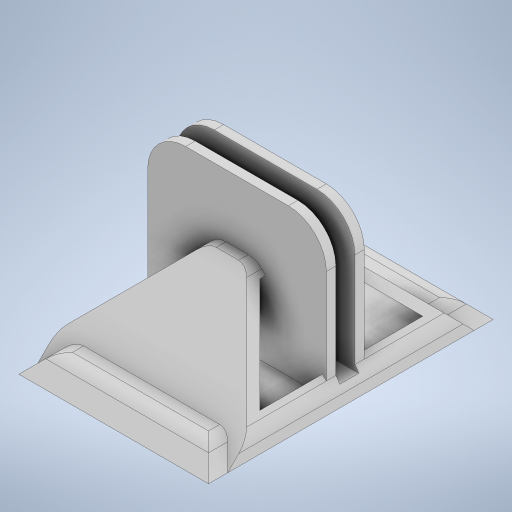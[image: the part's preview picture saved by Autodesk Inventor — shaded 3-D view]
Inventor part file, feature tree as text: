
AUTODESK INVENTOR PART (.ipt)
format: ipt  version: 2023.1 (Build 271208000, 208)  size: 363,520 bytes
history: native  units: mm
features: extrude x4, sketch x3, chamfer x3, projected_geometry x2, fillet x1, mirror x1
ambient origin geometry x8: Origin, YZ Plane, XZ Plane, XY Plane, X Axis, Y Axis, Z Axis, Center Point
bodies: Solid1 (feature_tree)
feature tree (14):
  sketch  "Sketch1"  dims[d0=50.0mm d1=55.0mm]
  extrude  "Extrusion1"  Depth=50.0mm
  extrude  "Extrusion2"  Depth=5.0mm TaperAngle=0.0deg
  chamfer  "Chamfer1"  Distance=20.0mm
  extrude  "Extrusion3"  Depth=2.5mm
  chamfer  "Chamfer2"  Distance=45.0mm
  chamfer  "Chamfer3"  Distance=5.0mm Angle=45.0deg
  fillet  "Fillet1"  Radius=20.0mm
  extrude  "Extrusion4"  Depth=5.0mm
  mirror  "Mirror1"
  sketch  "Sketch2"  dims[d2=5.0mm d3=5.0mm d4=0.0mm d5=20.0mm d6=0.0mm]
  projected_geometry  "Projected Loop1"
  sketch  "Sketch3"  dims[d7=20.0mm d8=2.0mm d9=45.0deg d10=75.0mm d12=45.0mm d13=0.0mm d14=5.0mm d15=2.0mm d16=45.0deg d17=20.0mm d18=2.0mm d19=45.0deg d22=5.0mm d23=2.5mm d24=35.0mm d25=10.0mm d26=2.5mm d27=0.0mm]
  projected_geometry  "Projected Loop2"
